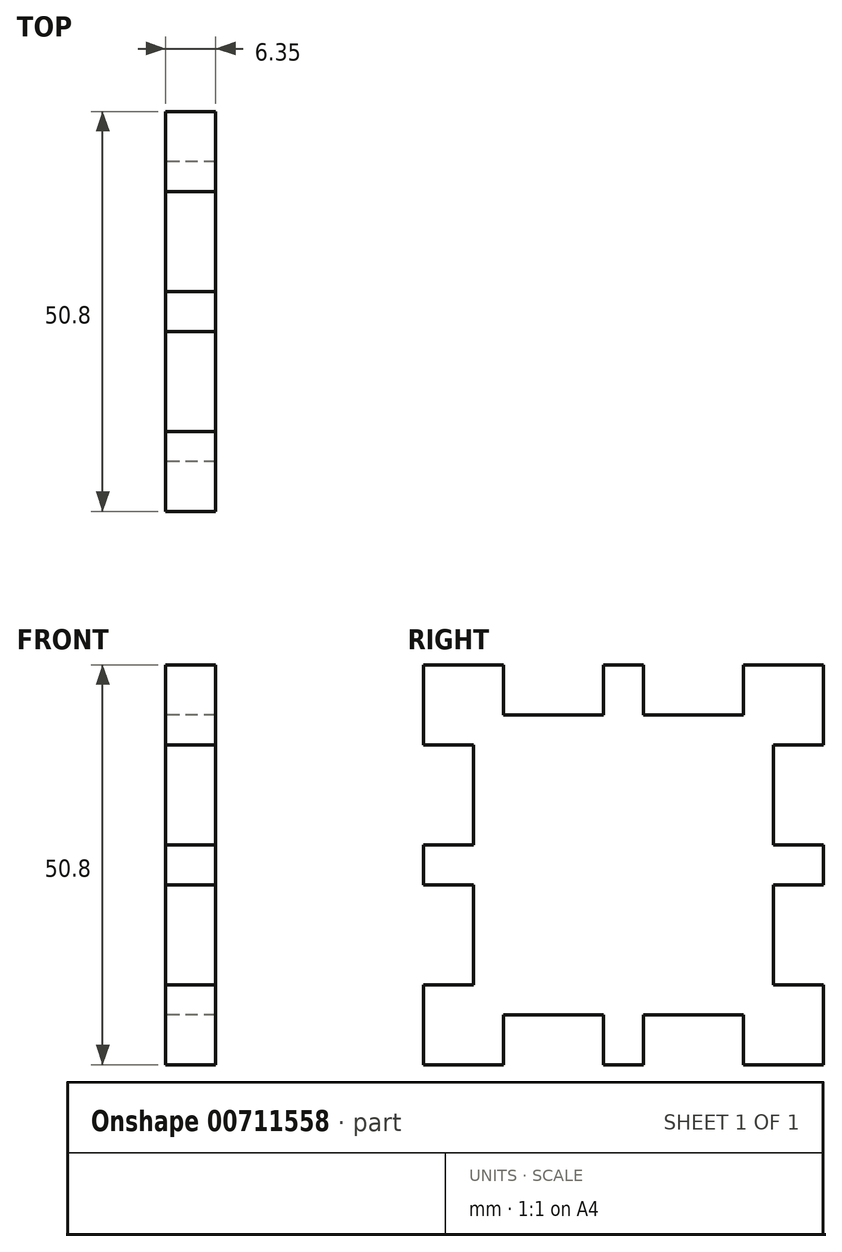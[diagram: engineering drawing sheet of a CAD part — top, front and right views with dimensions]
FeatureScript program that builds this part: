
annotation { "Feature Type Name" : "Feature", "Feature Type Description" : "" }
export const myFeature = defineFeature(function(context is Context, id is Id, definition is map)
    precondition{}
    {
        {
            var Q0;
            Q0=qCreatedBy(makeId("Front.planeOp"),FACE);
            var sketch = newSketch(context, id + "F0", { "sketchPlane" : qUnion([Q0])});
            skLineSegment(sketch, "E0.bottom", {"start": v(25.4, 25.4) * mm, "end": v(-25.4, 25.4) * mm});
            skLineSegment(sketch, "E0.top", {"start": v(25.4, -25.4) * mm, "end": v(-25.4, -25.4) * mm});
            skLineSegment(sketch, "E0.left", {"start": v(25.4, 25.4) * mm, "end": v(25.4, -25.4) * mm});
            skLineSegment(sketch, "E0.right", {"start": v(-25.4, 25.4) * mm, "end": v(-25.4, -25.4) * mm});
            skPoint(sketch, "E0.middle", {"position": v(0, 0) * mm});
            skSolve(sketch);
        }
        {
            var Q0;
            Q0=qCreatedBy(makeId("Right.planeOp"),FACE);
            var sketch = newSketch(context, id + "F1", { "sketchPlane" : qUnion([Q0])});
            skLineSegment(sketch, "E1", {"start": v(-15.24, 19.05) * mm, "end": v(-2.54, 19.05) * mm});
            skLineSegment(sketch, "E2", {"start": v(-15.24, 25.4) * mm, "end": v(-15.24, 19.05) * mm});
            skLineSegment(sketch, "E3", {"start": v(-2.54, 25.4) * mm, "end": v(-2.54, 19.05) * mm});
            skLineSegment(sketch, "E4", {"start": v(2.54, 25.4) * mm, "end": v(2.54, 19.05) * mm});
            skLineSegment(sketch, "E5", {"start": v(15.24, 25.4) * mm, "end": v(15.24, 19.05) * mm});
            skLineSegment(sketch, "E6.trimOffspring", {"start": v(2.54, 19.05) * mm, "end": v(15.24, 19.05) * mm});
            skLineSegment(sketch, "E7", {"start": v(15.24, 25.4) * mm, "end": v(25.4, 25.4) * mm});
            skLineSegment(sketch, "E8", {"start": v(25.4, 25.4) * mm, "end": v(25.4, 15.24) * mm});
            skLineSegment(sketch, "E9", {"start": v(25.4, 15.24) * mm, "end": v(19.05, 15.24) * mm});
            skLineSegment(sketch, "E10", {"start": v(19.05, 15.24) * mm, "end": v(19.05, 2.54) * mm});
            skLineSegment(sketch, "E11", {"start": v(19.05, 2.54) * mm, "end": v(25.4, 2.54) * mm});
            skLineSegment(sketch, "E12", {"start": v(25.4, 2.54) * mm, "end": v(25.4, -2.54) * mm});
            skLineSegment(sketch, "E13", {"start": v(25.4, -2.54) * mm, "end": v(19.05, -2.54) * mm});
            skLineSegment(sketch, "E14", {"start": v(19.05, -2.54) * mm, "end": v(19.05, -15.24) * mm});
            skLineSegment(sketch, "E15", {"start": v(19.05, -15.24) * mm, "end": v(25.4, -15.24) * mm});
            skLineSegment(sketch, "E16", {"start": v(25.4, -15.24) * mm, "end": v(25.4, -25.4) * mm});
            skLineSegment(sketch, "E17", {"start": v(25.4, -25.4) * mm, "end": v(15.24, -25.4) * mm});
            skLineSegment(sketch, "E18", {"start": v(15.24, -25.4) * mm, "end": v(15.24, -19.05) * mm});
            skLineSegment(sketch, "E19", {"start": v(15.24, -19.05) * mm, "end": v(2.54, -19.05) * mm});
            skLineSegment(sketch, "E20", {"start": v(2.54, -19.05) * mm, "end": v(2.54, -25.4) * mm});
            skLineSegment(sketch, "E21", {"start": v(2.54, -25.4) * mm, "end": v(-2.54, -25.4) * mm});
            skLineSegment(sketch, "E22", {"start": v(-2.54, -25.4) * mm, "end": v(-2.54, -19.05) * mm});
            skLineSegment(sketch, "E23", {"start": v(-2.54, -19.05) * mm, "end": v(-15.24, -19.05) * mm});
            skLineSegment(sketch, "E24", {"start": v(-15.24, -19.05) * mm, "end": v(-15.24, -25.4) * mm});
            skLineSegment(sketch, "E25", {"start": v(-15.24, -25.4) * mm, "end": v(-25.4, -25.4) * mm});
            skLineSegment(sketch, "E26", {"start": v(-25.4, -25.4) * mm, "end": v(-25.4, -15.24) * mm});
            skLineSegment(sketch, "E27", {"start": v(-25.4, -15.24) * mm, "end": v(-19.05, -15.24) * mm});
            skLineSegment(sketch, "E28", {"start": v(-19.05, -15.24) * mm, "end": v(-19.05, -2.54) * mm});
            skLineSegment(sketch, "E29", {"start": v(-19.05, -2.54) * mm, "end": v(-25.4, -2.54) * mm});
            skLineSegment(sketch, "E30", {"start": v(-25.4, -2.54) * mm, "end": v(-25.4, 2.54) * mm});
            skLineSegment(sketch, "E31", {"start": v(-25.4, 2.54) * mm, "end": v(-19.05, 2.54) * mm});
            skLineSegment(sketch, "E32", {"start": v(-19.05, 2.54) * mm, "end": v(-19.05, 15.24) * mm});
            skLineSegment(sketch, "E33", {"start": v(-19.05, 15.24) * mm, "end": v(-25.4, 15.24) * mm});
            skLineSegment(sketch, "E34", {"start": v(-25.4, 15.24) * mm, "end": v(-25.4, 25.4) * mm});
            skLineSegment(sketch, "E35", {"start": v(-25.4, 25.4) * mm, "end": v(-15.24, 25.4) * mm});
            skLineSegment(sketch, "E36", {"start": v(-2.54, 25.4) * mm, "end": v(2.54, 25.4) * mm});
            skSolve(sketch);
        }
        {
            var Q0;
            Q0=makeQuery(id+"F1.imprint","IMPRINT",FACE,{"disambiguationData":[TD([[makeQuery(id+"F1.imprint","IMPRINT",EDGE,{"derivedFrom":sQuery(id+"F1.wireOp",EDGE,"E1")}),-1.0]])]});
            extrude(context, id + "F2", {"entities" : qUnion([Q0]), "depth" : 6.35 * mm, "offsetDistance" : 25.4 * mm});
        }
    });
